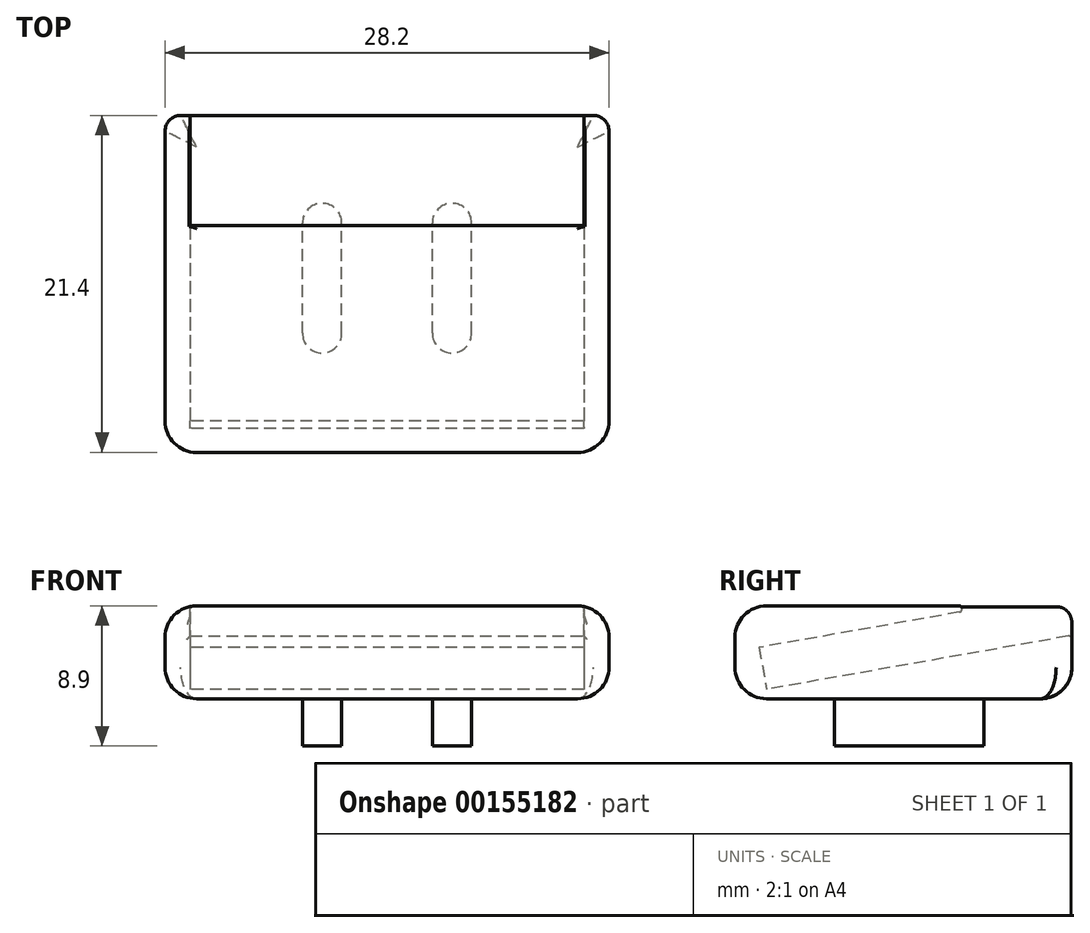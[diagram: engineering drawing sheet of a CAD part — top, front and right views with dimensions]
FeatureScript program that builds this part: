
annotation { "Feature Type Name" : "Feature", "Feature Type Description" : "" }
export const myFeature = defineFeature(function(context is Context, id is Id, definition is map)
    precondition{}
    {
        {
            var Q0;
            Q0=qCreatedBy(makeId("Top.planeOp"),FACE);
            var sketch = newSketch(context, id + "F0", { "sketchPlane" : qUnion([Q0])});
            skLineSegment(sketch, "E0.bottom", {"start": v(12.5, 16.05) * mm, "end": v(-12.5, 16.05) * mm});
            skLineSegment(sketch, "E0.top", {"start": v(12.5, -16.05) * mm, "end": v(-12.5, -16.05) * mm});
            skLineSegment(sketch, "E0.left", {"start": v(12.5, 16.05) * mm, "end": v(12.5, -16.05) * mm});
            skLineSegment(sketch, "E0.right", {"start": v(-12.5, 16.05) * mm, "end": v(-12.5, -16.05) * mm});
            skPoint(sketch, "E0.middle", {"position": v(0, 0) * mm});
            skSolve(sketch);
        }
        {
            var Q0;
            Q0=makeQuery(id+"F0.imprint","IMPRINT",FACE,{"disambiguationData":[TD([[makeQuery(id+"F0.imprint","IMPRINT",EDGE,{"derivedFrom":sQuery(id+"F0.wireOp",EDGE,"E0.bottom")}),1.0]])]});
            extrude(context, id + "F1", {"entities" : qUnion([Q0]), "endBound" : BoundingType.SYMMETRIC, "depth" : 2.7 * mm});
        }
        {
            var Q0;
            Q0=makeQuery(id+"F1.opExtrude","SWEPT_FACE",FACE,{"disambiguationData":[OSD([sQuery(id+"F0.wireOp",EDGE,"E0.top")])]});
            var sketch = newSketch(context, id + "F2", { "sketchPlane" : qUnion([Q0])});
            skLineSegment(sketch, "E1.0", {"start": v(14.1, 2.95) * mm, "end": v(-14.1, 2.95) * mm});
            skLineSegment(sketch, "E1.1", {"start": v(14.1, 2.95) * mm, "end": v(14.1, -2.95) * mm});
            skLineSegment(sketch, "E1.2", {"start": v(14.1, -2.95) * mm, "end": v(-14.1, -2.95) * mm});
            skLineSegment(sketch, "E1.3", {"start": v(-14.1, 2.95) * mm, "end": v(-14.1, -2.95) * mm});
            skSolve(sketch);
        }
        {
            var Q0;
            Q0 = qSketchRegion(id + "F2", true);
            extrude(context, id + "F3", {"entities" : qUnion([Q0]), "oppositeDirection" : true, "depth" : 21.4 * mm});
        }
        {
            var Q0;
            Q0=makeQuery(id+"F3.opExtrude","SWEPT_BODY",BODY,{"disambiguationData":[OSD([sQuery(id+"F2.wireOp",EDGE,"E1.0"),sQuery(id+"F2.wireOp",EDGE,"E1.1"),sQuery(id+"F2.wireOp",EDGE,"E1.2"),sQuery(id+"F2.wireOp",EDGE,"E1.3")])]});
            transform(context, id + "F4", {"entities" : qUnion([Q0]), "transformType" : TransformType.TRANSLATION_3D, "dx" : 0 * mm, "dy" : -2 * mm, "dz" : 0 * mm, "makeCopy" : false});
        }
        {
            var Q0;
            Q0=makeQuery(id+"F1.opExtrude","SWEPT_BODY",BODY,{"disambiguationData":[OSD([sQuery(id+"F0.wireOp",EDGE,"E0.bottom"),sQuery(id+"F0.wireOp",EDGE,"E0.top"),sQuery(id+"F0.wireOp",EDGE,"E0.left"),sQuery(id+"F0.wireOp",EDGE,"E0.right")])]});
            var Q1;
            Q1=makeQuery(id+"F1.opExtrude","CAP_EDGE",EDGE,{"disambiguationData":[OSD([sQuery(id+"F0.wireOp",EDGE,"E0.top")])],"isStart":true});
            transform(context, id + "F5", {"entities" : qUnion([Q0]), "transformType" : TransformType.ROTATION, "transformAxis" : qUnion([Q1]), "angle" : 10 * degree, "oppositeDirection" : true, "makeCopy" : false});
        }
        {
            var Q0;
            Q0=makeQuery(id+"F1.opExtrude","SWEPT_BODY",BODY,{"disambiguationData":[OSD([sQuery(id+"F0.wireOp",EDGE,"E0.bottom"),sQuery(id+"F0.wireOp",EDGE,"E0.top"),sQuery(id+"F0.wireOp",EDGE,"E0.left"),sQuery(id+"F0.wireOp",EDGE,"E0.right")])]});
            transform(context, id + "F6", {"entities" : qUnion([Q0]), "transformType" : TransformType.TRANSLATION_3D, "dx" : 0 * mm, "dy" : 0 * mm, "dz" : -1 * mm, "makeCopy" : false});
        }
        {
            var Q0;
            Q0=makeQuery(id+"F1.opExtrude","SWEPT_BODY",BODY,{"disambiguationData":[OSD([sQuery(id+"F0.wireOp",EDGE,"E0.bottom"),sQuery(id+"F0.wireOp",EDGE,"E0.top"),sQuery(id+"F0.wireOp",EDGE,"E0.left"),sQuery(id+"F0.wireOp",EDGE,"E0.right")])]});
            var Q1;
            Q1=makeQuery(id+"F3.opExtrude","SWEPT_BODY",BODY,{"disambiguationData":[OSD([sQuery(id+"F2.wireOp",EDGE,"E1.0"),sQuery(id+"F2.wireOp",EDGE,"E1.1"),sQuery(id+"F2.wireOp",EDGE,"E1.2"),sQuery(id+"F2.wireOp",EDGE,"E1.3")])]});
            booleanBodies(context, id + "F7", {"operationType" : BooleanOperationType.SUBTRACTION, "tools" : qUnion([Q0]), "targets" : qUnion([Q1]), "keepTools" : true});
        }
        {
            var Q0;
            Q0=makeQuery(id+"F3.opExtrude","SWEPT_FACE",FACE,{"disambiguationData":[OSD([sQuery(id+"F2.wireOp",EDGE,"E1.2")])]});
            var sketch = newSketch(context, id + "F8", { "sketchPlane" : qUnion([Q0])});
            skCircle(sketch, "E2", {"center": v(-4.12, 10.48) * mm, "radius": 1.25 * mm});
            skCircle(sketch, "E3.1.0.0", {"center": v(4.13, 10.48) * mm, "radius": 1.25 * mm});
            skLineSegment(sketch, "E3.direction1", {"start": v(-4.12, 10.48) * mm, "end": v(4.13, 10.48) * mm, "construction": true});
            skLineSegment(sketch, "E4", {"start": v(-14.1, 7.35) * mm, "end": v(14.1, 7.35) * mm, "construction": true});
            skLineSegment(sketch, "E5", {"start": v(0, -3.35) * mm, "end": v(0, 18.05) * mm, "construction": true});
            skPoint(sketch, "E6", {"position": v(0, 7.35) * mm});
            skLineSegment(sketch, "E7", {"start": v(-4.12, 10.48) * mm, "end": v(-4.12, 3.48) * mm});
            skLineSegment(sketch, "E8.MirrorCS", {"start": v(4.13, 10.48) * mm, "end": v(4.13, 3.48) * mm});
            skArc(sketch, "E9.0.startCap", {"start": v(-5.37, 10.48) * mm, "mid": v(-4.12, 11.73) * mm, "end": v(-2.87, 10.48) * mm});
            skArc(sketch, "E9.0.endCap", {"start": v(-2.87, 3.48) * mm, "mid": v(-4.12, 2.23) * mm, "end": v(-5.37, 3.48) * mm});
            skLineSegment(sketch, "E9.0.left", {"start": v(-2.87, 10.48) * mm, "end": v(-2.87, 3.48) * mm});
            skLineSegment(sketch, "E9.0.right", {"start": v(-5.37, 10.48) * mm, "end": v(-5.37, 3.48) * mm});
            skArc(sketch, "E9.1.startCap", {"start": v(2.88, 10.48) * mm, "mid": v(4.13, 11.73) * mm, "end": v(5.38, 10.48) * mm});
            skArc(sketch, "E9.1.endCap", {"start": v(5.38, 3.48) * mm, "mid": v(4.13, 2.23) * mm, "end": v(2.88, 3.48) * mm});
            skLineSegment(sketch, "E9.1.left", {"start": v(5.38, 10.48) * mm, "end": v(5.38, 3.48) * mm});
            skLineSegment(sketch, "E9.1.right", {"start": v(2.88, 10.48) * mm, "end": v(2.88, 3.48) * mm});
            skSolve(sketch);
        }
        {
            var Q0;
            Q0 = qSketchRegion(id + "F8", true);
            extrude(context, id + "F9", {"entities" : qUnion([Q0]), "operationType" : NewBodyOperationType.ADD, "depth" : 3 * mm});
        }
        {
            var Q0;
            Q0=makeQuery(id+"F7.opBoolean","INTERSECT",EDGE,{"derivedFrom":[makeQuery(id+"F1.opExtrude","CAP_FACE",FACE,{"disambiguationData":[OSD([sQuery(id+"F0.wireOp",EDGE,"E0.bottom"),sQuery(id+"F0.wireOp",EDGE,"E0.top"),sQuery(id+"F0.wireOp",EDGE,"E0.left"),sQuery(id+"F0.wireOp",EDGE,"E0.right")])],"isStart":false}),makeQuery(id+"F3.opExtrude","SWEPT_FACE",FACE,{"disambiguationData":[OSD([sQuery(id+"F2.wireOp",EDGE,"E1.0")])]})]});
            var Q1;
            Q1=makeQuery(id+"F7.opBoolean","INTERSECT",EDGE,{"derivedFrom":[makeQuery(id+"F1.opExtrude","SWEPT_FACE",FACE,{"disambiguationData":[OSD([sQuery(id+"F0.wireOp",EDGE,"E0.right")])]}),makeQuery(id+"F3.opExtrude","SWEPT_FACE",FACE,{"disambiguationData":[OSD([sQuery(id+"F2.wireOp",EDGE,"E1.0")])]})]});
            var Q2;
            Q2=makeQuery(id+"F7.opBoolean","INTERSECT",EDGE,{"derivedFrom":[makeQuery(id+"F1.opExtrude","SWEPT_FACE",FACE,{"disambiguationData":[OSD([sQuery(id+"F0.wireOp",EDGE,"E0.left")])]}),makeQuery(id+"F3.opExtrude","SWEPT_FACE",FACE,{"disambiguationData":[OSD([sQuery(id+"F2.wireOp",EDGE,"E1.0")])]})]});
            var Q3;
            Q3=makeQuery(id+"F7.opBoolean","INTERSECT",EDGE,{"derivedFrom":[makeQuery(id+"F1.opExtrude","SWEPT_FACE",FACE,{"disambiguationData":[OSD([sQuery(id+"F0.wireOp",EDGE,"E0.left")])]}),makeQuery(id+"F3.opExtrude","CAP_FACE",FACE,{"disambiguationData":[OSD([sQuery(id+"F2.wireOp",EDGE,"E1.0"),sQuery(id+"F2.wireOp",EDGE,"E1.1"),sQuery(id+"F2.wireOp",EDGE,"E1.2"),sQuery(id+"F2.wireOp",EDGE,"E1.3")])],"isStart":false})]});
            var Q4;
            Q4=makeQuery(id+"F7.opBoolean","INTERSECT",EDGE,{"derivedFrom":[makeQuery(id+"F1.opExtrude","SWEPT_FACE",FACE,{"disambiguationData":[OSD([sQuery(id+"F0.wireOp",EDGE,"E0.right")])]}),makeQuery(id+"F3.opExtrude","CAP_FACE",FACE,{"disambiguationData":[OSD([sQuery(id+"F2.wireOp",EDGE,"E1.0"),sQuery(id+"F2.wireOp",EDGE,"E1.1"),sQuery(id+"F2.wireOp",EDGE,"E1.2"),sQuery(id+"F2.wireOp",EDGE,"E1.3")])],"isStart":false})]});
            var Q5;
            Q5=makeQuery(id+"F7.opBoolean","INTERSECT",EDGE,{"derivedFrom":[makeQuery(id+"F1.opExtrude","CAP_FACE",FACE,{"disambiguationData":[OSD([sQuery(id+"F0.wireOp",EDGE,"E0.bottom"),sQuery(id+"F0.wireOp",EDGE,"E0.top"),sQuery(id+"F0.wireOp",EDGE,"E0.left"),sQuery(id+"F0.wireOp",EDGE,"E0.right")])],"isStart":true}),makeQuery(id+"F3.opExtrude","CAP_FACE",FACE,{"disambiguationData":[OSD([sQuery(id+"F2.wireOp",EDGE,"E1.0"),sQuery(id+"F2.wireOp",EDGE,"E1.1"),sQuery(id+"F2.wireOp",EDGE,"E1.2"),sQuery(id+"F2.wireOp",EDGE,"E1.3")])],"isStart":false})]});
            fillet(context, id + "F10", {"entities" : qUnion([Q0, Q1, Q2, Q3, Q4, Q5]), "radius" : .2 * mm, "tangentPropagation" : true, "allowEdgeOverflow" : false});
        }
        {
            var Q0;
            Q0=makeQuery(id+"F3.opExtrude","CAP_EDGE",EDGE,{"disambiguationData":[OSD([sQuery(id+"F2.wireOp",EDGE,"E1.0")])],"isStart":true});
            var Q1;
            Q1=makeQuery(id+"F3.opExtrude","SWEPT_EDGE",EDGE,{"disambiguationData":[OSD([sQuery(id+"F2.wireOp",EDGE,"E1.0"),sQuery(id+"F2.wireOp",EDGE,"E1.3")])]});
            var Q2;
            Q2=makeQuery(id+"F3.opExtrude","SWEPT_EDGE",EDGE,{"disambiguationData":[OSD([sQuery(id+"F2.wireOp",EDGE,"E1.0"),sQuery(id+"F2.wireOp",EDGE,"E1.1")])]});
            var Q3;
            Q3=makeQuery(id+"F3.opExtrude","SWEPT_EDGE",EDGE,{"disambiguationData":[OSD([sQuery(id+"F2.wireOp",EDGE,"E1.1"),sQuery(id+"F2.wireOp",EDGE,"E1.2")])]});
            var Q4;
            Q4=makeQuery(id+"F3.opExtrude","SWEPT_EDGE",EDGE,{"disambiguationData":[OSD([sQuery(id+"F2.wireOp",EDGE,"E1.2"),sQuery(id+"F2.wireOp",EDGE,"E1.3")])]});
            var Q5;
            Q5=makeQuery(id+"F3.opExtrude","CAP_EDGE",EDGE,{"disambiguationData":[OSD([sQuery(id+"F2.wireOp",EDGE,"E1.2")])],"isStart":true});
            var Q6;
            Q6=makeQuery(id+"F3.opExtrude","CAP_EDGE",EDGE,{"disambiguationData":[OSD([sQuery(id+"F2.wireOp",EDGE,"E1.1")])],"isStart":true});
            var Q7;
            Q7=makeQuery(id+"F3.opExtrude","CAP_EDGE",EDGE,{"disambiguationData":[OSD([sQuery(id+"F2.wireOp",EDGE,"E1.3")])],"isStart":true});
            var Q8;
            Q8=makeQuery(id+"F3.opExtrude","CAP_EDGE",EDGE,{"disambiguationData":[OSD([sQuery(id+"F2.wireOp",EDGE,"E1.2")])],"isStart":false});
            fillet(context, id + "F11", {"entities" : qUnion([Q0, Q1, Q2, Q3, Q4, Q5, Q6, Q7, Q8]), "radius" : 2 * mm, "tangentPropagation" : true, "allowEdgeOverflow" : false});
        }
        {
            var Q0;
            Q0=makeQuery(id+"F3.opExtrude","CAP_EDGE",EDGE,{"disambiguationData":[OSD([sQuery(id+"F2.wireOp",EDGE,"E1.1")])],"isStart":false});
            var Q1;
            Q1=makeQuery(id+"F3.opExtrude","CAP_EDGE",EDGE,{"disambiguationData":[OSD([sQuery(id+"F2.wireOp",EDGE,"E1.3")])],"isStart":false});
            fillet(context, id + "F12", {"entities" : qUnion([Q0, Q1]), "radius" : 1 * mm, "tangentPropagation" : true, "allowEdgeOverflow" : false});
        }
        {
            var Q0;
            Q0=makeQuery(id+"F1.opExtrude","SWEPT_BODY",BODY,{"disambiguationData":[OSD([sQuery(id+"F0.wireOp",EDGE,"E0.bottom"),sQuery(id+"F0.wireOp",EDGE,"E0.top"),sQuery(id+"F0.wireOp",EDGE,"E0.left"),sQuery(id+"F0.wireOp",EDGE,"E0.right")])]});
            deleteBodies(context, id + "F13", {"entities" : qUnion([Q0])});
        }
    });
